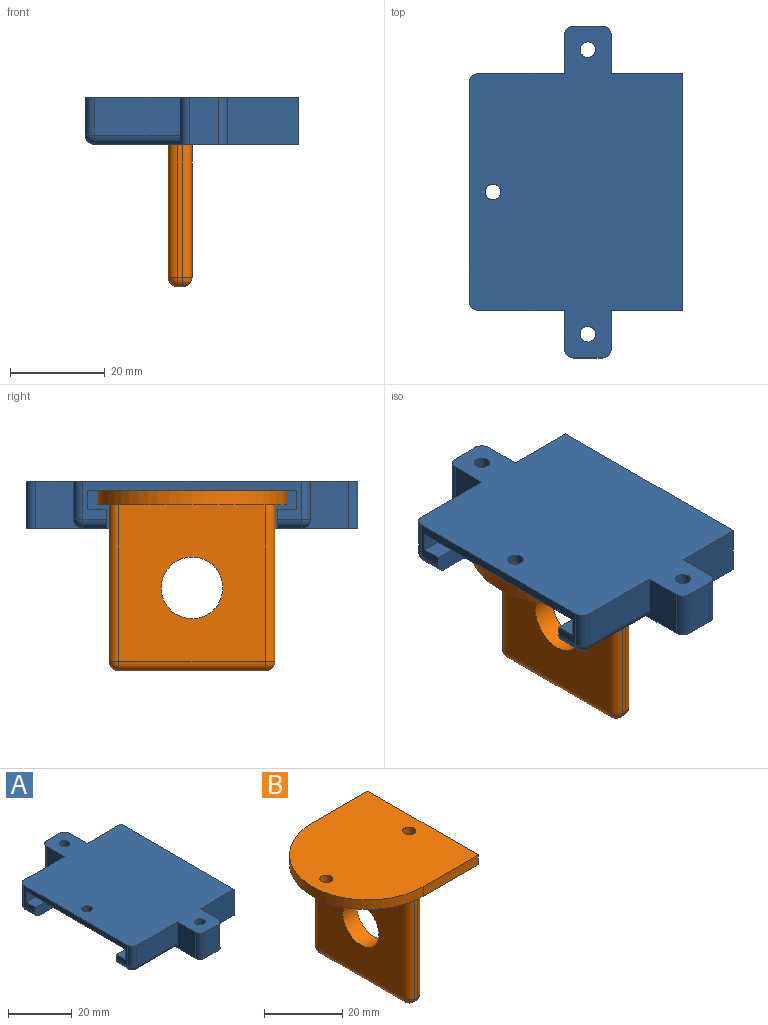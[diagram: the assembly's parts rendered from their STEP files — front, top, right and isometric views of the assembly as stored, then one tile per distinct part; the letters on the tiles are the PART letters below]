
ASSEMBLY  parts=2 mates=1
PART A: 39 faces, bbox 45x70x10 mm
  f0: plane 10x10mm, normal (-1,0,0), area 80.9mm2, adj f1,f12,f13,f27,f32
  f1: plane 18x8mm, normal (0,1,0), area 144mm2, adj f0,f12,f27,f28
  f2: plane 46x8mm, normal (-1,0,0), area 120mm2, adj f12,f14,f15,f16,f17,f18,f19,f20
  f3: plane 18x8mm, normal (0,-1,0), area 144mm2, adj f4,f12,f35,f38
  f4: plane 10x10mm, normal (-1,0,0), area 80.9mm2, adj f3,f12,f13,f34,f35
  f5: plane 10x6mm, normal (0,-1,0), area 60mm2, adj f12,f13,f33,f34
  f6: plane 10x8mm, normal (1,0,0), area 80mm2, adj f7,f12,f13,f33
  f7: plane 15x10mm, normal (0,-1,0), area 150mm2, adj f6,f8,f12,f13
  f8: plane 50x10mm, normal (1,0,0), area 500mm2, adj f7,f9,f12,f13
  f9: plane 15x10mm, normal (0,1,0), area 150mm2, adj f8,f10,f12,f13
  f10: plane 10x8mm, normal (1,0,0), area 80mm2, adj f9,f12,f13,f31
  f11: plane 10x6mm, normal (0,1,0), area 60mm2, adj f12,f13,f31,f32
  f12: plane 70x45mm, normal (0,0,1), area 2419.2mm2, adj f0,f1,f2,f3,f4,f5,f6,f7
  f13: plane 70x43mm, normal (0,0,-1), area 787.7mm2, adj f0,f4,f5,f6,f7,f8,f9,f10
  f14: plane 44x40mm, normal (0,0,-1), area 1751.4mm2, adj f2,f15,f20,f21,f22
  f15: plane 40x4mm, normal (0,-1,0), area 160mm2, adj f2,f14,f16,f21
  f16: plane 40x4mm, normal (0,0,1), area 160mm2, adj f2,f15,f17,f21
  f17: plane 40x4mm, normal (0,-1,0), area 159.1mm2, adj f2,f13,f16,f21,f30
  f18: plane 40x4mm, normal (0,1,0), area 159.1mm2, adj f2,f13,f19,f21,f36
  f19: plane 40x4mm, normal (0,0,1), area 160mm2, adj f2,f18,f20,f21
  f20: plane 40x4mm, normal (0,1,0), area 160mm2, adj f2,f14,f19,f21
  f21: plane 44x8mm, normal (-1,0,0), area 320mm2, adj f13,f14,f15,f16,f17,f18,f19,f20
  f22: cylinder r=1.65mm len=3.3mm, axis (0,0,1), area 20.7mm2, adj f12,f14
  f23: cylinder r=1.65mm len=7.3mm, axis (0,0,-1), area 75.7mm2, adj f12,f24
  f24: cone r=1.65mm half-angle=45deg, axis (0,0,-1), area 72mm2, adj f13,f23
  f25: cylinder r=1.65mm len=7.3mm, axis (0,0,-1), area 75.7mm2, adj f12,f26
  f26: cone r=1.65mm half-angle=45deg, axis (0,0,-1), area 72mm2, adj f13,f25
  f27: cylinder r=2mm len=18mm, axis (-1,0,0), area 56.5mm2, adj f0,f1,f13,f29
  f28: cylinder r=2mm len=8mm, axis (0,0,-1), area 25.1mm2, adj f1,f2,f12,f29
  f29: sphere r=2mm, area 6.3mm2, adj f27,f28,f30
  f30: cylinder r=2mm len=5mm, axis (0,-1,0), area 15.7mm2, adj f2,f13,f17,f29
  f31: cylinder r=2mm len=10mm, axis (0,0,-1), area 31.4mm2, adj f10,f11,f12,f13
  f32: cylinder r=2mm len=10mm, axis (0,0,-1), area 31.4mm2, adj f0,f11,f12,f13
  f33: cylinder r=2mm len=10mm, axis (0,0,-1), area 31.4mm2, adj f5,f6,f12,f13
  f34: cylinder r=2mm len=10mm, axis (0,0,-1), area 31.4mm2, adj f4,f5,f12,f13
  f35: cylinder r=2mm len=18mm, axis (1,0,0), area 56.5mm2, adj f3,f4,f13,f37
  f36: cylinder r=2mm len=5mm, axis (0,-1,0), area 15.7mm2, adj f2,f13,f18,f37
  f37: sphere r=2mm, area 6.3mm2, adj f35,f36,f38
  f38: cylinder r=2mm len=8mm, axis (0,0,-1), area 25.1mm2, adj f2,f3,f12,f37
PART B: 26 faces, bbox 40x40x38 mm
  f0: plane 31x1mm, normal (0,0,-1), area 31mm2, adj f15,f20,f21,f25
  f1: plane 33x1mm, normal (0,1,0), area 33mm2, adj f11,f14,f15,f16
  f2: plane 33x1mm, normal (0,-1,0), area 33mm2, adj f11,f19,f22,f25
  f3: cylinder r=6.5mm len=13mm, axis (-1,0,0), area 204.2mm2, adj f4,f5
  f4: plane 33x31mm, normal (1,0,0), area 890.3mm2, adj f3,f11,f14,f19,f20
  f5: plane 33x31mm, normal (-1,0,0), area 890.3mm2, adj f3,f11,f16,f21,f22
  f6: cylinder r=20mm len=40mm, axis (0,0,-1), area 188.5mm2, adj f7,f9,f10,f11
  f7: plane 20x3mm, normal (0,-1,0), area 60mm2, adj f6,f8,f10,f11
  f8: plane 40x3mm, normal (1,0,0), area 120mm2, adj f7,f9,f10,f11
  f9: plane 20x3mm, normal (0,1,0), area 60mm2, adj f6,f8,f10,f11
  f10: plane 40x40mm, normal (0,0,1), area 1411.2mm2, adj f6,f7,f8,f9,f12,f13
  f11: plane 40x40mm, normal (0,0,-1), area 1239.6mm2, adj f1,f2,f4,f5,f6,f7,f8,f9
  f12: cylinder r=1.65mm len=3.3mm, axis (0,0,1), area 31.1mm2, adj f10,f11
  f13: cylinder r=1.65mm len=3.3mm, axis (0,0,1), area 31.1mm2, adj f10,f11
  f14: cylinder r=2mm len=33mm, axis (0,0,-1), area 103.7mm2, adj f1,f4,f11,f17
  f15: cylinder r=2mm len=2mm, axis (-1,0,0), area 3.1mm2, adj f0,f1,f17,f18
  f16: cylinder r=2mm len=33mm, axis (0,0,1), area 103.7mm2, adj f1,f5,f11,f18
  f17: sphere r=2mm, area 6.3mm2, adj f14,f15,f20
  f18: sphere r=2mm, area 6.3mm2, adj f15,f16,f21
  f19: cylinder r=2mm len=33mm, axis (0,0,1), area 103.7mm2, adj f2,f4,f11,f23
  f20: cylinder r=2mm len=31mm, axis (0,-1,0), area 97.4mm2, adj f0,f4,f17,f23
  f21: cylinder r=2mm len=31mm, axis (0,1,0), area 97.4mm2, adj f0,f5,f18,f24
  f22: cylinder r=2mm len=33mm, axis (0,0,-1), area 103.7mm2, adj f2,f5,f11,f24
  f23: sphere r=2mm, area 6.3mm2, adj f19,f20,f25
  f24: sphere r=2mm, area 6.3mm2, adj f21,f22,f25
  f25: cylinder r=2mm len=2mm, axis (-1,0,0), area 3.1mm2, adj f0,f2,f23,f24
PLACE A t=(-27.41,-17.73,-29.7)mm
PLACE B t=(-32.41,-17.73,-21.7)mm
MATE fastened A.f22 <-> B.f12  axis (0,0,-1) through (-44.91,-0.23,16.3)mm
